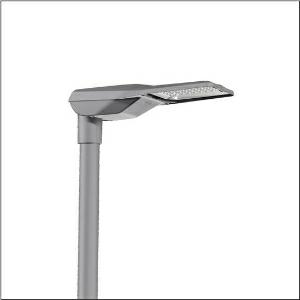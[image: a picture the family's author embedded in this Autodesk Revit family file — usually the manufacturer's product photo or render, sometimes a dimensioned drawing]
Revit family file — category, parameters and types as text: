
# Revit family: streetlight_sl_21_iq_mini___st1_0a_5xe2d31d08gb_54bd
name_source: partatom
category: Lighting Fixtures
units: mm (PartAtom-declared; Revit-internal decimal feet)

## family parameters
Cut with Voids When Loaded = No
Host = Face
Light Source = No
Part Type = Normal
Room Calculation Point = No
Round Connector Dimension = Use Diameter
Shared = No

## types (1)
- --- (1 x LED, 5680 lm, 37.1 W, 3000K)
    Apparent Load = 37 VA
    CIE Flux Codes = 37 72 97 100 100
    Color Rendering = 70
    Color Temperature = 3000K
    Default Elevation = 1800 mm
    Description = Streetlight SL 21 iQ mini, mast luminaire, primary light control with lens, of PMMA, primary optical cover: cover, of toughened safety glass, transparent, light distribution: ST1.0a, light emission: direct distribution, primary light characteristic: asymmetric, installation type: post-top, side-entry, LED, High Power LED, rated luminous flux: 5.680lm, luminous efficacy: 153lm/W, light colour: 730, colour temperature: 3000K, control gear: iQ-Comfort, control: Auto-Match, Temp-Guard, Lumen-Switch, Night-Set, Smart-Wire, Light-Fading, Desk-Remote (wireless, voltage-free reading and setting of iQ features in the workshop via application-optimized NFC function/RFID function), optimised constant luminous flux control (CLO 2.0), pre-setting: linear dimming characteristic, mains connection: 220..240V, AC, 50/60Hz, start of lifetime: 37W, end of service life: 39W, reduction: 18W, luminaire housing, of diecast aluminium, powder-coated, SITECO metallic grey (DB 702S), corrosivity category C5 high according to DIN EN ISO 12944, please order mast flange separately, inclination adjustable: 0°, 5°, 10°, 15°, sealing non-destructively replaceable, multi-level sealing system, length: 628mm, width: 235mm, height: 110mm, mast flange for spigot size: 42mm (side-entry): 5XC10008XM4, 60/48mm (side-entry/post-top): 5XC10108XM2, 76/60mm (side-entry/post-top): 5XC10108XM1, mounting height: 4..8m, protection rating (complete): IP66, insulation class (complete): insulation class II (safety insulation), certification: CE, ENEC, ENEC+, VDE, impact resistance: IK10, permissible operating ambient temperature for outdoor applications: -40..+50°C, standard-compliant lighting for roads and squares, packaging unit: 1 piece

Light Distribution: ST1.0a
    Height = 110 mm
    Lamp = 1 x LED
    Lamp Light Flux = 5680 lm
    Lamp Power = 37.1 W
    Lamp count = 1
    Length = 625 mm
    Luminous efficacy = 153 lm/W
    Manufacturer = Siteco
    ModVariant = No
    Model = 5XE2D31D08GB
    Number of Poles = 1
    OnlyDefault = Yes
    Power Factor = 1
    Product Name = Streetlight SL 21 iQ mini | ST1.0a
    Product group = mast luminaire | pylon top
    ProductGroupID = 6100
    Protection Class = Protection class II
    Protection Degree = IP 66
    RLX_Detail_Level = 1
    RLX_Emergency_Light_Flux = 0 lm
    RLX_Emergency_Type = 0
    RLX_Emergency_Type_DB = No
    RlxData = <blob elided: 26381 chars, md5=5ad20ea9>
    Socket = socket
    Standby Power = 0 W
    System Light Flux = 5680 lm
    System Power = 37 W
    Type Comments = factory setting: luminous flux: 100 % | dim-lin: 254 | 385 mA
    Type Image = l_1003519.jpg
    URL = http://relux.com
    VarID = @adj_186419
    Voltage = 0 V
    Weight = 0.00 kg
    Width = 234 mm

## geometry (parser evidence)
native form markers: Blend x4, Sweep x9
no freeform markers — native parametric forms only
